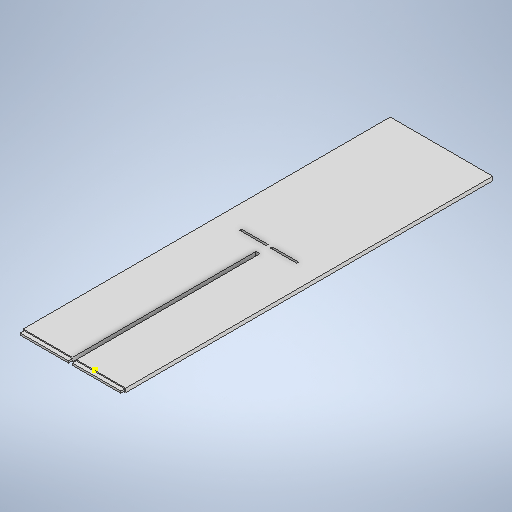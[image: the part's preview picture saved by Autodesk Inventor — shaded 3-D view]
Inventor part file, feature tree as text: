
AUTODESK INVENTOR PART (.ipt)
format: ipt  version: 2025.2 (Build 292293000, 293)  size: 407,552 bytes
history: native  units: mm
features: sketch x15, extrude x14, projected_geometry x3
ambient origin geometry x8: Origin, YZ Plane, XZ Plane, XY Plane, X Axis, Y Axis, Z Axis, Center Point
bodies: Solid1 (feature_tree)
feature tree (32):
  extrude  "Extrusion1"  Depth=447.675mm
  extrude  "Extrusion2"  Depth=4.7625mm TaperAngle=0.0deg
  extrude  "Extrusion3"  Depth=10.0mm TaperAngle=0.0deg
  extrude  "Extrusion4"  Depth=158.838mm TaperAngle=0.0deg
  sketch  "Sketch5"  dims[d25=4.763mm d26=223.837mm d27=0.0mm]
  extrude  "Extrusion5"  Depth=223.837mm TaperAngle=0.0deg
  extrude  "Extrusion6"  Depth=15.0mm TaperAngle=0.0deg
  extrude  "Extrusion7"  Depth=2.374mm TaperAngle=0.0deg
  extrude  "Extrusion8"  Depth=2.374mm TaperAngle=0.0deg
  extrude  "Extrusion9"  Depth=4.763mm
  extrude  "Extrusion10"  Depth=10.0mm TaperAngle=0.0deg
  extrude  "Extrusion11"  Depth=10.0mm TaperAngle=0.0deg
  extrude  "Extrusion12"  [1 undecoded]
  extrude  "Extrusion13"  [1 undecoded]
  extrude  "Extrusion14"  [1 undecoded]
  sketch  "Sketch1"  dims[d0=50.0mm d1=447.675mm]
  sketch  "Sketch2"  dims[d2=4.7625mm d3=0.0mm d9=4.7625mm d10=0.0mm]
  sketch  "Sketch3"  dims[d11=25.0mm d18=10.0mm d19=0.0mm]
  sketch  "Sketch4"  dims[d20=10.0mm d21=0.0mm d22=158.838mm d23=0.0mm]
  sketch  "Sketch6"  dims[d28=15.0mm d29=0.0mm d30=15.0mm d31=0.0mm]
  projected_geometry  "Projected Loop1"
  sketch  "Sketch8"  dims[d35=2.374mm d36=10.0mm d37=0.0mm]
  sketch  "Sketch9"  dims[d43=2.374mm d44=10.0mm d45=0.0mm]
  projected_geometry  "Projected Loop2"
  sketch  "Sketch10"  dims[d46=4.763mm d47=0.0mm d48=37.5mm]
  projected_geometry  "Projected Loop3"
  sketch  "Sketch14"  dims[d49=37.5mm d50=10.0mm d51=0.0mm]
  sketch  "Sketch17"  dims[d53=10.0mm d54=0.0mm d57=10.0mm d58=0.0mm]
  sketch  "Sketch18"
  sketch  "Sketch19"
  sketch  "Sketch20"
  sketch  "Sketch21"
note: 3 required parameter values undecoded (feature->parameter linkage not recoverable at this tier; creation-order binding heuristic only, values carry confidence <= 0.55)
